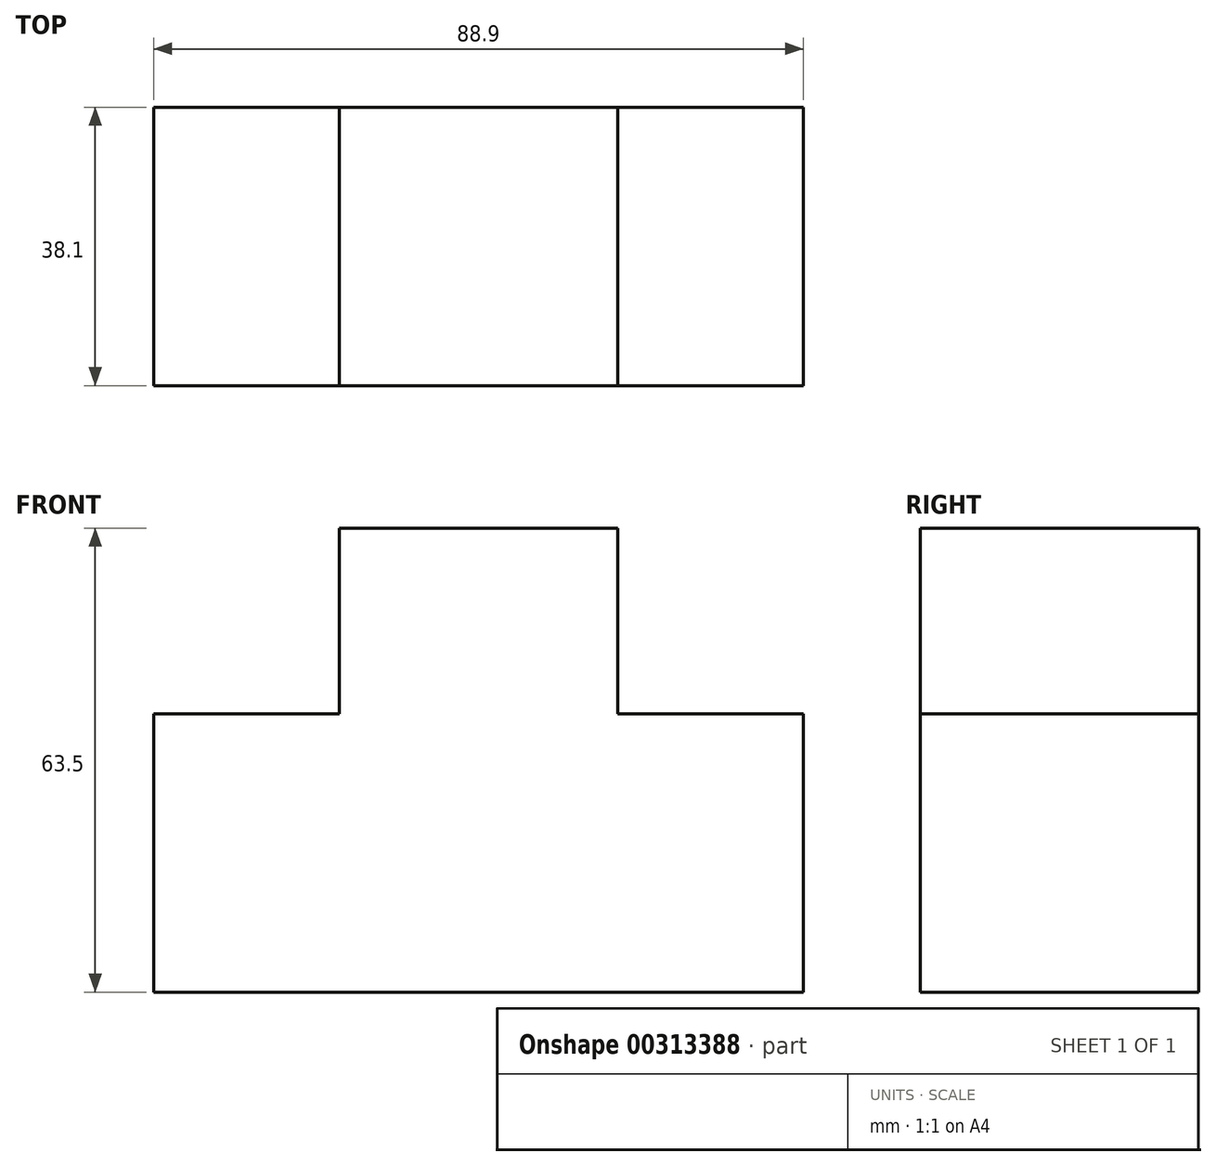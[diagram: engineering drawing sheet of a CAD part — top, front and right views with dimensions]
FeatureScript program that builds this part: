
annotation { "Feature Type Name" : "Feature", "Feature Type Description" : "" }
export const myFeature = defineFeature(function(context is Context, id is Id, definition is map)
    precondition{}
    {
        {
            var Q0;
            Q0=qCreatedBy(makeId("Front.planeOp"),FACE);
            var sketch = newSketch(context, id + "F0", { "sketchPlane" : qUnion([Q0])});
            skLineSegment(sketch, "E0", {"start": v(-42.44, -46.58) * mm, "end": v(46.46, -46.58) * mm});
            skLineSegment(sketch, "E1", {"start": v(46.46, -46.58) * mm, "end": v(46.46, -8.48) * mm});
            skLineSegment(sketch, "E2", {"start": v(46.46, -8.48) * mm, "end": v(21.06, -8.48) * mm});
            skLineSegment(sketch, "E3", {"start": v(21.06, -8.48) * mm, "end": v(21.06, 16.92) * mm});
            skLineSegment(sketch, "E4", {"start": v(21.06, 16.92) * mm, "end": v(-17.04, 16.92) * mm});
            skLineSegment(sketch, "E5", {"start": v(-17.04, 16.92) * mm, "end": v(-17.04, -8.48) * mm});
            skLineSegment(sketch, "E6", {"start": v(-17.04, -8.48) * mm, "end": v(-42.44, -8.48) * mm});
            skLineSegment(sketch, "E7", {"start": v(-42.44, -8.48) * mm, "end": v(-42.44, -46.58) * mm});
            skSolve(sketch);
        }
        {
            var Q0;
            Q0=makeQuery(id+"F0.imprint","IMPRINT",FACE,{"disambiguationData":[TD([[makeQuery(id+"F0.imprint","IMPRINT",EDGE,{"derivedFrom":sQuery(id+"F0.wireOp",EDGE,"E0")}),1.0]])]});
            extrude(context, id + "F1", {"entities" : qUnion([Q0]), "depth" : 38.1 * mm});
        }
    });
